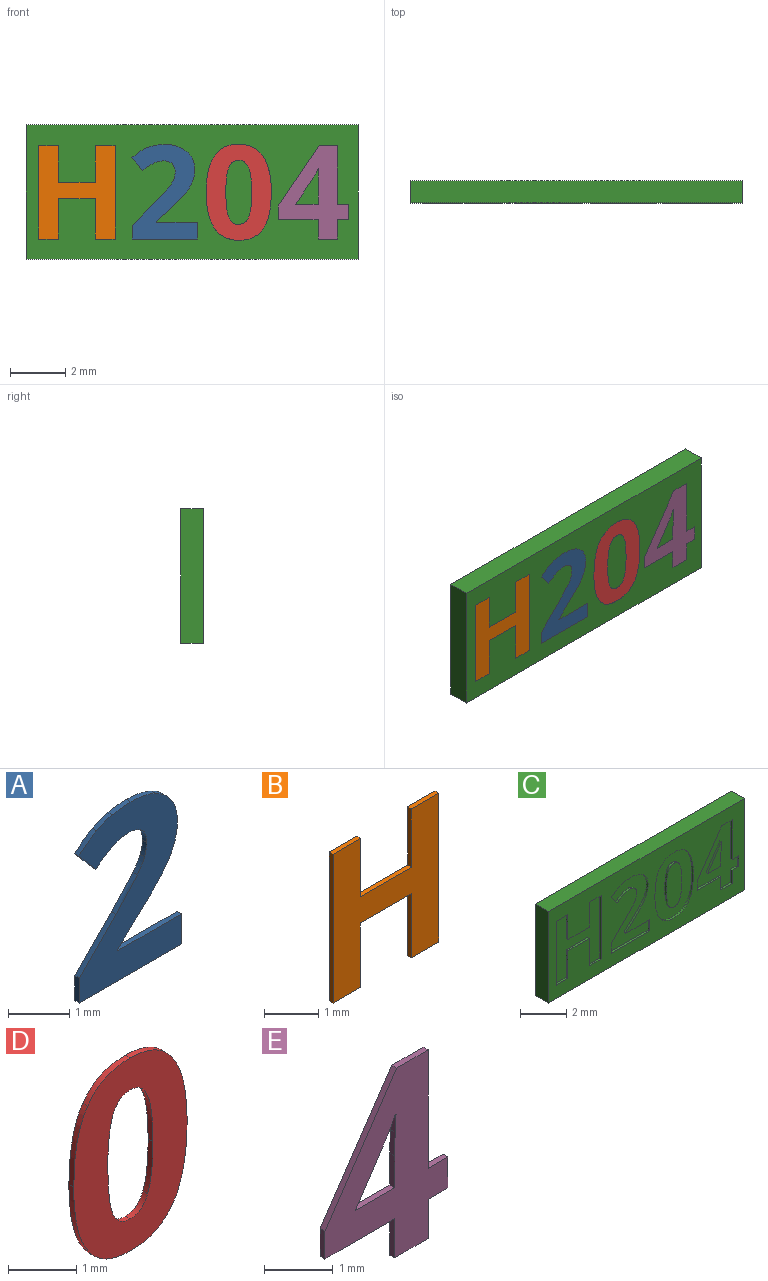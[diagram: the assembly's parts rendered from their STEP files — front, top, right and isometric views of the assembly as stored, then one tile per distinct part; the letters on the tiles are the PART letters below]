
ASSEMBLY  parts=5 mates=4
PART A: 26 faces, bbox 2.4x0.1x3.4 mm
  f0: plane 3.42x2.37mm, normal (0,-1,0), area 4.2mm2, adj f1,f2,f3,f4,f5,f6,f7,f8
  f1: plane 1.47x0.1mm, normal (0,0,1), area 0.1mm2, adj f0,f2,f22,f24
  f2: plane 0.1x0.03mm, normal (1,0,0), area 0mm2, adj f0,f1,f3,f22
  f3: plane 0.43x0.41mm, normal (0.69,0,-0.73), area 0.1mm2, adj f0,f2,f4,f22
  f4: extruded ~0.61x0.61mm, area 0.1mm2, adj f0,f3,f5,f22
  f5: extruded ~0.42x0.25mm, area 0mm2, adj f0,f4,f6,f22
  f6: extruded ~0.44x0.1mm, area 0mm2, adj f0,f5,f7,f22
  f7: extruded ~0.48x0.13mm, area 0.1mm2, adj f0,f6,f8,f22
  f8: extruded ~0.38x0.32mm, area 0.1mm2, adj f0,f7,f9,f22
  f9: extruded ~0.56x0.12mm, area 0.1mm2, adj f0,f8,f10,f22
  f10: extruded ~0.43x0.1mm, area 0mm2, adj f0,f9,f11,f22
  f11: extruded ~0.36x0.13mm, area 0mm2, adj f0,f10,f12,f22
  f12: extruded ~0.41x0.3mm, area 0.1mm2, adj f0,f11,f13,f22
  f13: plane 0.46x0.39mm, normal (-0.76,0,-0.65), area 0.1mm2, adj f0,f12,f14,f22
  f14: extruded ~0.39x0.26mm, area 0mm2, adj f0,f13,f15,f22
  f15: extruded ~0.38x0.1mm, area 0mm2, adj f0,f14,f16,f22
  f16: extruded ~0.3x0.1mm, area 0mm2, adj f0,f15,f17,f22
  f17: extruded ~0.3x0.11mm, area 0mm2, adj f0,f16,f18,f22
  f18: extruded ~0.26x0.1mm, area 0mm2, adj f0,f17,f19,f22
  f19: extruded ~0.28x0.17mm, area 0mm2, adj f0,f18,f20,f22
  f20: extruded ~0.53x0.49mm, area 0.1mm2, adj f0,f19,f21,f22
  f21: plane 0.86x0.85mm, normal (-0.71,0,0.7), area 0.1mm2, adj f0,f20,f22,f23
  f22: plane 3.42x2.37mm, normal (0,1,0), area 4.2mm2, adj f1,f2,f3,f4,f5,f6,f7,f8
  f23: plane 0.5x0.1mm, normal (-1,0,0), area 0mm2, adj f0,f21,f22,f25
  f24: plane 0.6x0.1mm, normal (1,0,0), area 0.1mm2, adj f0,f1,f22,f25
  f25: plane 2.36x0.1mm, normal (0,0,-1), area 0.2mm2, adj f0,f22,f23,f24
PART B: 14 faces, bbox 2.8x0.1x3.4 mm
  f0: plane 3.37x2.76mm, normal (0,-1,0), area 5.6mm2, adj f1,f2,f3,f4,f5,f6,f7,f8
  f1: plane 0.71x0.1mm, normal (0,0,1), area 0.1mm2, adj f0,f2,f10,f12
  f2: plane 1.32x0.1mm, normal (-1,0,0), area 0.1mm2, adj f0,f1,f3,f10
  f3: plane 1.33x0.1mm, normal (0,0,1), area 0.1mm2, adj f0,f2,f4,f10
  f4: plane 1.32x0.1mm, normal (1,0,0), area 0.1mm2, adj f0,f3,f5,f10
  f5: plane 0.72x0.1mm, normal (0,0,1), area 0.1mm2, adj f0,f4,f6,f10
  f6: plane 3.37x0.1mm, normal (-1,0,0), area 0.3mm2, adj f0,f5,f7,f10
  f7: plane 0.72x0.1mm, normal (0,0,-1), area 0.1mm2, adj f0,f6,f8,f10
  f8: plane 1.46x0.1mm, normal (1,0,0), area 0.1mm2, adj f0,f7,f9,f10
  f9: plane 1.33x0.1mm, normal (0,0,-1), area 0.1mm2, adj f0,f8,f10,f11
  f10: plane 3.37x2.76mm, normal (0,1,0), area 5.6mm2, adj f1,f2,f3,f4,f5,f6,f7,f8
  f11: plane 1.46x0.1mm, normal (-1,0,0), area 0.1mm2, adj f0,f9,f10,f13
  f12: plane 3.37x0.1mm, normal (1,0,0), area 0.3mm2, adj f0,f1,f10,f13
  f13: plane 0.71x0.1mm, normal (0,0,-1), area 0.1mm2, adj f0,f10,f11,f12
PART C: 82 faces, bbox 12x0.8x4.9 mm
  f0: plane 12x4.85mm, normal (0,-1,0), area 36.7mm2, adj f1,f2,f3,f4,f6,f7,f8,f9
  f1: plane 12x0.8mm, normal (0,0,-1), area 9.6mm2, adj f0,f2,f4,f5
  f2: plane 4.85x0.8mm, normal (1,0,0), area 3.9mm2, adj f0,f1,f3,f5
  f3: plane 12x0.8mm, normal (0,0,1), area 9.6mm2, adj f0,f2,f4,f5
  f4: plane 4.85x0.8mm, normal (-1,0,0), area 3.9mm2, adj f0,f1,f3,f5
  f5: plane 12x4.85mm, normal (0,1,0), area 58.2mm2, adj f1,f2,f3,f4
  f6: plane 0.55x0.1mm, normal (-1,0,0), area 0.1mm2, adj f0,f7,f23,f24
  f7: plane 0.41x0.1mm, normal (0,0,-1), area 0mm2, adj f0,f6,f8,f24
  f8: plane 2.12x0.1mm, normal (-1,0,0), area 0.2mm2, adj f0,f7,f9,f24
  f9: plane 0.66x0.1mm, normal (0,0,-1), area 0.1mm2, adj f0,f8,f10,f24
  f10: plane 2.18x1.48mm, normal (0.83,0,-0.56), area 0.3mm2, adj f0,f9,f11,f24
  f11: plane 0.5x0.1mm, normal (1,0,0), area 0mm2, adj f0,f10,f12,f24
  f12: plane 1.44x0.1mm, normal (0,0,1), area 0.1mm2, adj f0,f11,f13,f24
  f13: plane 0.7x0.1mm, normal (1,0,0), area 0.1mm2, adj f0,f12,f14,f24
  f14: plane 0.7x0.1mm, normal (0,0,1), area 0.1mm2, adj f0,f13,f15,f24
  f15: plane 0.7x0.1mm, normal (-1,0,0), area 0.1mm2, adj f0,f14,f23,f24
  f16: plane 0.81x0.1mm, normal (0,0,-1), area 0.1mm2, adj f17,f22,f24,f25
  f17: plane 0.93x0.62mm, normal (-0.83,0,0.55), area 0.1mm2, adj f16,f18,f24,f25
  f18: extruded ~0.37x0.21mm, area 0mm2, adj f17,f19,f24,f25
  f19: plane 0.1x0.02mm, normal (0,0,1), area 0mm2, adj f18,f20,f24,f25
  f20: extruded ~0.32x0.1mm, area 0mm2, adj f19,f21,f24,f25
  f21: extruded ~0.42x0.1mm, area 0mm2, adj f20,f22,f24,f25
  f22: plane 0.57x0.1mm, normal (1,0,0), area 0.1mm2, adj f16,f21,f24,f25
  f23: plane 0.41x0.1mm, normal (0,0,1), area 0mm2, adj f0,f6,f15,f24
  f24: plane 3.37x2.54mm, normal (0,-1,0), area 4.3mm2, adj f6,f7,f8,f9,f10,f11,f12,f13
  f25: plane 1.3x0.84mm, normal (0,-1,0), area 0.5mm2, adj f16,f17,f18,f19,f20,f21,f22
  f26: extruded ~1.3x0.3mm, area 0.1mm2, adj f0,f27,f41,f42
  f27: extruded ~0.88x0.44mm, area 0.1mm2, adj f0,f26,f28,f42
  f28: extruded ~0.89x0.42mm, area 0.1mm2, adj f0,f27,f29,f42
  f29: extruded ~1.32x0.29mm, area 0.1mm2, adj f0,f28,f30,f42
  f30: extruded ~1.29x0.3mm, area 0.1mm2, adj f0,f29,f31,f42
  f31: extruded ~0.88x0.44mm, area 0.1mm2, adj f0,f30,f32,f42
  f32: extruded ~0.89x0.42mm, area 0.1mm2, adj f0,f31,f41,f42
  f33: extruded ~0.89x0.11mm, area 0.1mm2, adj f34,f40,f42,f43
  f34: extruded ~0.36x0.27mm, area 0mm2, adj f33,f35,f42,f43
  f35: extruded ~0.36x0.27mm, area 0mm2, adj f34,f36,f42,f43
  f36: extruded ~0.89x0.11mm, area 0.1mm2, adj f35,f37,f42,f43
  f37: extruded ~0.89x0.11mm, area 0.1mm2, adj f36,f38,f42,f43
  f38: extruded ~0.36x0.27mm, area 0mm2, adj f37,f39,f42,f43
  f39: extruded ~0.36x0.27mm, area 0mm2, adj f38,f40,f42,f43
  f40: extruded ~0.89x0.11mm, area 0.1mm2, adj f33,f39,f42,f43
  f41: extruded ~1.31x0.29mm, area 0.1mm2, adj f0,f26,f32,f42
  f42: plane 3.47x2.36mm, normal (0,-1,0), area 5mm2, adj f26,f27,f28,f29,f30,f31,f32,f33
  f43: plane 2.32x0.94mm, normal (0,-1,0), area 1.8mm2, adj f33,f34,f35,f36,f37,f38,f39,f40
  f44: plane 0.6x0.1mm, normal (-1,0,0), area 0.1mm2, adj f0,f45,f67,f68
  f45: plane 1.47x0.1mm, normal (0,0,-1), area 0.1mm2, adj f0,f44,f46,f68
  f46: plane 0.1x0.03mm, normal (-1,0,0), area 0mm2, adj f0,f45,f47,f68
  f47: plane 0.43x0.41mm, normal (-0.69,0,0.73), area 0.1mm2, adj f0,f46,f48,f68
  f48: extruded ~0.61x0.61mm, area 0.1mm2, adj f0,f47,f49,f68
  f49: extruded ~0.42x0.25mm, area 0mm2, adj f0,f48,f50,f68
  f50: extruded ~0.44x0.1mm, area 0mm2, adj f0,f49,f51,f68
  f51: extruded ~0.48x0.13mm, area 0.1mm2, adj f0,f50,f52,f68
  f52: extruded ~0.38x0.32mm, area 0.1mm2, adj f0,f51,f53,f68
  f53: extruded ~0.56x0.12mm, area 0.1mm2, adj f0,f52,f54,f68
  f54: extruded ~0.43x0.1mm, area 0mm2, adj f0,f53,f55,f68
  f55: extruded ~0.36x0.13mm, area 0mm2, adj f0,f54,f56,f68
  f56: extruded ~0.41x0.3mm, area 0.1mm2, adj f0,f55,f57,f68
  f57: plane 0.46x0.39mm, normal (0.76,0,0.65), area 0.1mm2, adj f0,f56,f58,f68
  f58: extruded ~0.39x0.26mm, area 0mm2, adj f0,f57,f59,f68
  f59: extruded ~0.38x0.1mm, area 0mm2, adj f0,f58,f60,f68
  f60: extruded ~0.3x0.1mm, area 0mm2, adj f0,f59,f61,f68
  f61: extruded ~0.3x0.11mm, area 0mm2, adj f0,f60,f62,f68
  f62: extruded ~0.26x0.1mm, area 0mm2, adj f0,f61,f63,f68
  f63: extruded ~0.28x0.17mm, area 0mm2, adj f0,f62,f64,f68
  f64: extruded ~0.53x0.49mm, area 0.1mm2, adj f0,f63,f65,f68
  f65: plane 0.86x0.85mm, normal (0.71,0,-0.7), area 0.1mm2, adj f0,f64,f66,f68
  f66: plane 0.5x0.1mm, normal (1,0,0), area 0mm2, adj f0,f65,f67,f68
  f67: plane 2.36x0.1mm, normal (0,0,1), area 0.2mm2, adj f0,f44,f66,f68
  f68: plane 3.42x2.37mm, normal (0,-1,0), area 4.2mm2, adj f44,f45,f46,f47,f48,f49,f50,f51
  f69: plane 3.37x0.1mm, normal (-1,0,0), area 0.3mm2, adj f0,f70,f80,f81
  f70: plane 0.71x0.1mm, normal (0,0,-1), area 0.1mm2, adj f0,f69,f71,f81
  f71: plane 1.32x0.1mm, normal (1,0,0), area 0.1mm2, adj f0,f70,f72,f81
  f72: plane 1.33x0.1mm, normal (0,0,-1), area 0.1mm2, adj f0,f71,f73,f81
  f73: plane 1.32x0.1mm, normal (-1,0,0), area 0.1mm2, adj f0,f72,f74,f81
  f74: plane 0.72x0.1mm, normal (0,0,-1), area 0.1mm2, adj f0,f73,f75,f81
  f75: plane 3.37x0.1mm, normal (1,0,0), area 0.3mm2, adj f0,f74,f76,f81
  f76: plane 0.72x0.1mm, normal (0,0,1), area 0.1mm2, adj f0,f75,f77,f81
  f77: plane 1.46x0.1mm, normal (-1,0,0), area 0.1mm2, adj f0,f76,f78,f81
  f78: plane 1.33x0.1mm, normal (0,0,1), area 0.1mm2, adj f0,f77,f79,f81
  f79: plane 1.46x0.1mm, normal (1,0,0), area 0.1mm2, adj f0,f78,f80,f81
  f80: plane 0.71x0.1mm, normal (0,0,1), area 0.1mm2, adj f0,f69,f79,f81
  f81: plane 3.37x2.76mm, normal (0,-1,0), area 5.6mm2, adj f69,f70,f71,f72,f73,f74,f75,f76
PART D: 18 faces, bbox 2.4x0.1x3.5 mm
  f0: plane 3.47x2.36mm, normal (0,-1,0), area 5mm2, adj f1,f2,f3,f4,f5,f6,f7,f8
  f1: extruded ~0.88x0.44mm, area 0.1mm2, adj f0,f2,f11,f13
  f2: extruded ~0.89x0.42mm, area 0.1mm2, adj f0,f1,f3,f11
  f3: extruded ~1.32x0.29mm, area 0.1mm2, adj f0,f2,f4,f11
  f4: extruded ~1.29x0.3mm, area 0.1mm2, adj f0,f3,f5,f11
  f5: extruded ~0.88x0.44mm, area 0.1mm2, adj f0,f4,f11,f12
  f6: extruded ~0.36x0.27mm, area 0mm2, adj f0,f7,f11,f16
  f7: extruded ~0.36x0.27mm, area 0mm2, adj f0,f6,f8,f11
  f8: extruded ~0.89x0.11mm, area 0.1mm2, adj f0,f7,f9,f11
  f9: extruded ~0.89x0.11mm, area 0.1mm2, adj f0,f8,f10,f11
  f10: extruded ~0.36x0.27mm, area 0mm2, adj f0,f9,f11,f15
  f11: plane 3.47x2.36mm, normal (0,1,0), area 5mm2, adj f1,f2,f3,f4,f5,f6,f7,f8
  f12: extruded ~0.89x0.42mm, area 0.1mm2, adj f0,f5,f11,f14
  f13: extruded ~1.3x0.3mm, area 0.1mm2, adj f0,f1,f11,f14
  f14: extruded ~1.31x0.29mm, area 0.1mm2, adj f0,f11,f12,f13
  f15: extruded ~0.36x0.27mm, area 0mm2, adj f0,f10,f11,f17
  f16: extruded ~0.89x0.11mm, area 0.1mm2, adj f0,f6,f11,f17
  f17: extruded ~0.89x0.11mm, area 0.1mm2, adj f0,f11,f15,f16
PART E: 20 faces, bbox 2.5x0.1x3.4 mm
  f0: plane 3.37x2.54mm, normal (0,-1,0), area 4.3mm2, adj f1,f2,f3,f4,f5,f6,f7,f8
  f1: plane 0.41x0.1mm, normal (0,0,1), area 0mm2, adj f0,f2,f13,f15
  f2: plane 2.12x0.1mm, normal (1,0,0), area 0.2mm2, adj f0,f1,f3,f13
  f3: plane 0.66x0.1mm, normal (0,0,1), area 0.1mm2, adj f0,f2,f4,f13
  f4: plane 2.18x1.48mm, normal (-0.83,0,0.56), area 0.3mm2, adj f0,f3,f5,f13
  f5: plane 0.5x0.1mm, normal (-1,0,0), area 0mm2, adj f0,f4,f6,f13
  f6: plane 1.44x0.1mm, normal (0,0,-1), area 0.1mm2, adj f0,f5,f7,f13
  f7: plane 0.7x0.1mm, normal (-1,0,0), area 0.1mm2, adj f0,f6,f8,f13
  f8: plane 0.7x0.1mm, normal (0,0,-1), area 0.1mm2, adj f0,f7,f13,f14
  f9: plane 0.93x0.62mm, normal (0.83,0,-0.55), area 0.1mm2, adj f0,f10,f13,f18
  f10: extruded ~0.37x0.21mm, area 0mm2, adj f0,f9,f11,f13
  f11: plane 0.1x0.02mm, normal (0,0,-1), area 0mm2, adj f0,f10,f12,f13
  f12: extruded ~0.32x0.1mm, area 0mm2, adj f0,f11,f13,f17
  f13: plane 3.37x2.54mm, normal (0,1,0), area 4.3mm2, adj f1,f2,f3,f4,f5,f6,f7,f8
  f14: plane 0.7x0.1mm, normal (1,0,0), area 0.1mm2, adj f0,f8,f13,f16
  f15: plane 0.55x0.1mm, normal (1,0,0), area 0.1mm2, adj f0,f1,f13,f16
  f16: plane 0.41x0.1mm, normal (0,0,-1), area 0mm2, adj f0,f13,f14,f15
  f17: extruded ~0.42x0.1mm, area 0mm2, adj f0,f12,f13,f19
  f18: plane 0.81x0.1mm, normal (0,0,1), area 0.1mm2, adj f0,f9,f13,f19
  f19: plane 0.57x0.1mm, normal (-1,0,0), area 0.1mm2, adj f0,f13,f17,f18
PLACE A t=(-2.52,0.37,-0.03)mm
PLACE B t=(-0.08,0.37,-0.03)mm
PLACE C t=(-0.02,0.37,-0.03)mm
PLACE D t=(-1.18,0.37,-0.03)mm
PLACE E t=(2.91,0.37,-0.03)mm
MATE fastened B.f0 <-> C.f0  axis (0,-1,0) through (-5.56,-0.43,-1.73)mm
MATE fastened D.f0 <-> C.f43  axis (0,-1,0) through (1.67,-0.43,-1.2)mm
MATE fastened A.f0 <-> C.f0  axis (0,-1,0) through (-2.19,-0.43,-1.73)mm
MATE fastened E.f0 <-> C.f0  axis (0,-1,0) through (4.53,-0.43,-1.73)mm
